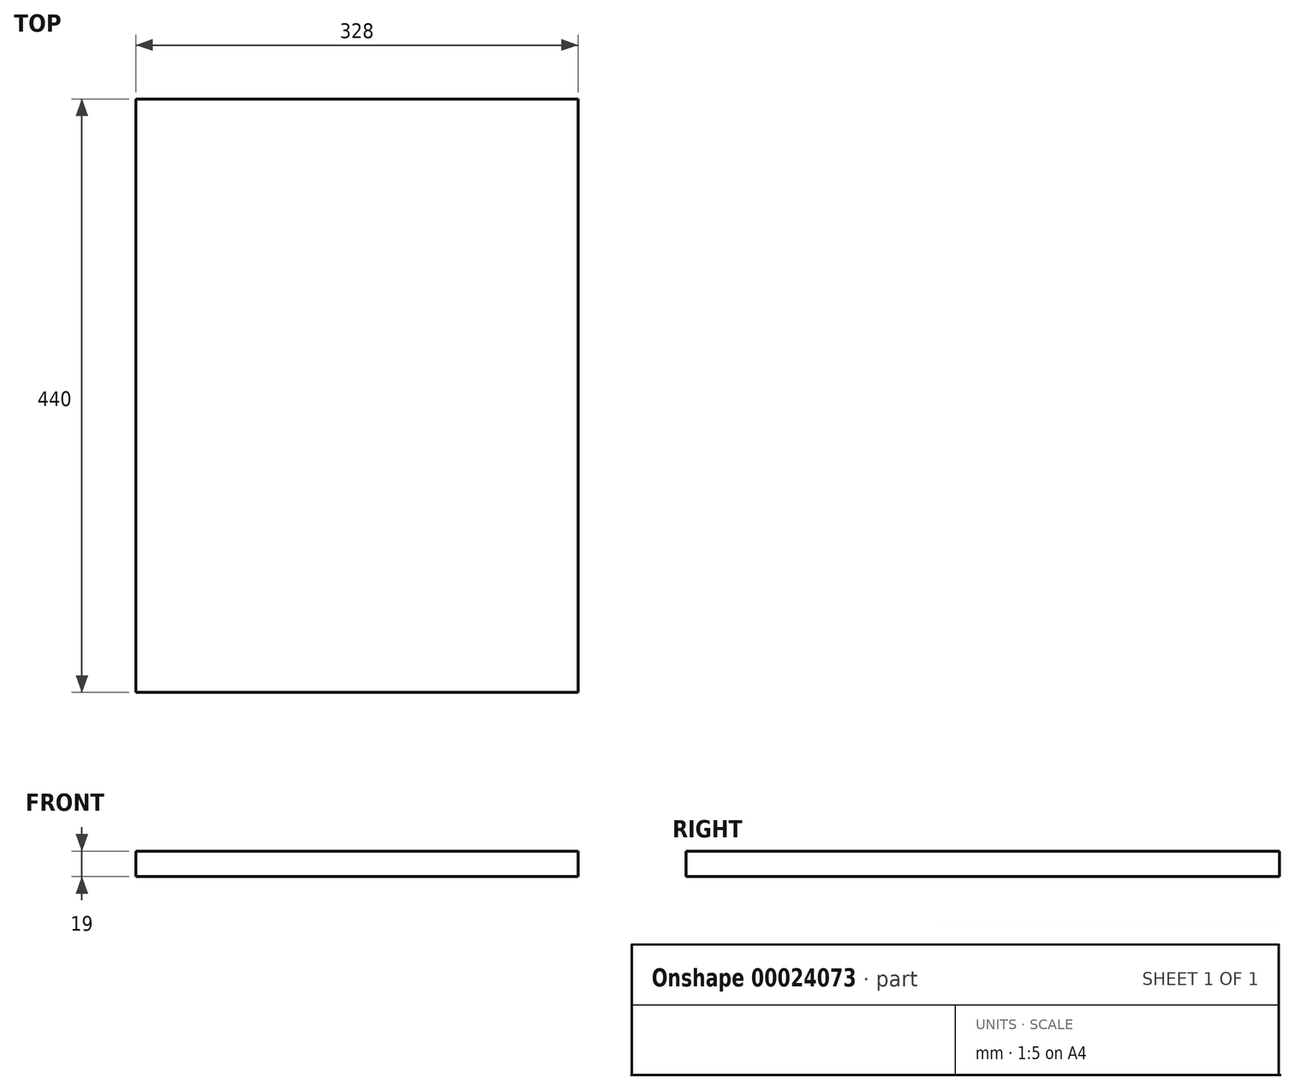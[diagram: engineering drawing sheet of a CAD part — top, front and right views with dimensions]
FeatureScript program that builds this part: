
annotation { "Feature Type Name" : "Feature", "Feature Type Description" : "" }
export const myFeature = defineFeature(function(context is Context, id is Id, definition is map)
    precondition{}
    {
        {
            var Q0;
            Q0=qCreatedBy(makeId("Top.planeOp"),FACE);
            var sketch = newSketch(context, id + "F0", { "sketchPlane" : qUnion([Q0])});
            skLineSegment(sketch, "E0.bottom", {"start": v(-70.96, 65.05) * mm, "end": v(257.04, 65.05) * mm});
            skLineSegment(sketch, "E0.top", {"start": v(-70.96, -374.95) * mm, "end": v(257.04, -374.95) * mm});
            skLineSegment(sketch, "E0.left", {"start": v(-70.96, 65.05) * mm, "end": v(-70.96, -374.95) * mm});
            skLineSegment(sketch, "E0.right", {"start": v(257.04, 65.05) * mm, "end": v(257.04, -374.95) * mm});
            skSolve(sketch);
        }
        {
            var Q0;
            Q0=qSketchRegion(id+"F0",true);
            extrude(context, id + "F1", {"entities" : qUnion([Q0]), "depth" : 19 * mm});
        }
    });
